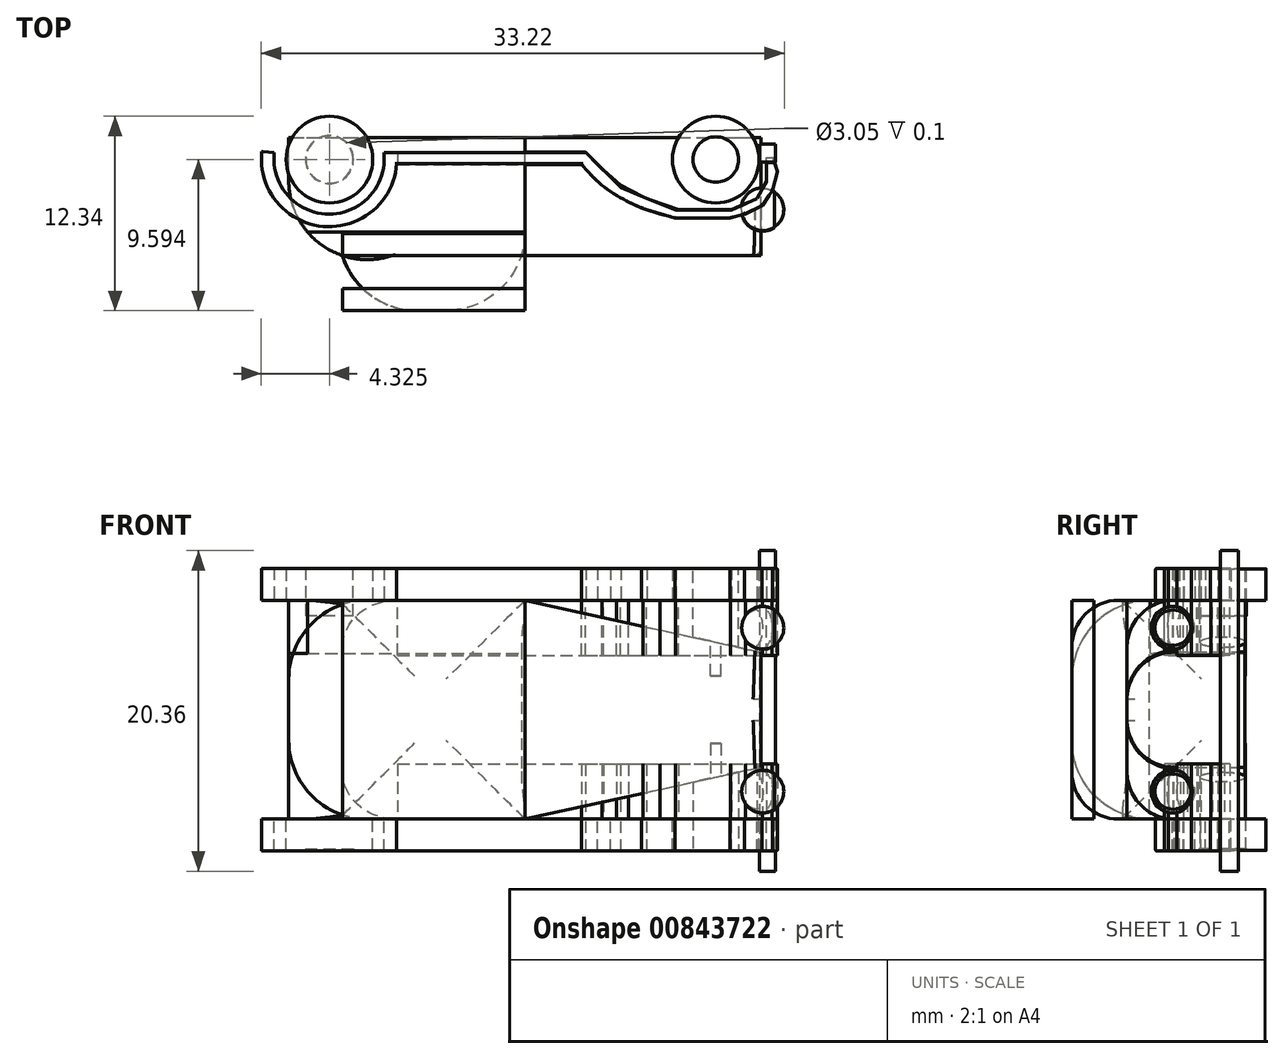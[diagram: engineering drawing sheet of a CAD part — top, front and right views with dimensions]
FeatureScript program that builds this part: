
annotation { "Feature Type Name" : "Feature", "Feature Type Description" : "" }
export const myFeature = defineFeature(function(context is Context, id is Id, definition is map)
    precondition{}
    {
        {
            var Q0;
            Q0=qCreatedBy(makeId("Front.planeOp"),FACE);
            var sketch = newSketch(context, id + "F0", { "sketchPlane" : qUnion([Q0])});
            skLineSegment(sketch, "E0", {"start": v(-15, 0) * mm, "end": v(-15, -6.95) * mm});
            skLineSegment(sketch, "E1", {"start": v(-15, -6.95) * mm, "end": v(0, -6.95) * mm});
            skLineSegment(sketch, "E2", {"start": v(0, -6.95) * mm, "end": v(15, -3.65) * mm});
            skPoint(sketch, "E3.end.orphan", {"position": v(14.2, 0) * mm});
            skLineSegment(sketch, "E4", {"start": v(15, -3.65) * mm, "end": v(15, 0) * mm});
            skLineSegment(sketch, "E5.MirrorCS", {"start": v(0, 6.95) * mm, "end": v(15, 3.65) * mm});
            skLineSegment(sketch, "E6.MirrorCS", {"start": v(-15, 6.95) * mm, "end": v(0, 6.95) * mm});
            skLineSegment(sketch, "E7.MirrorCS", {"start": v(-15, 0) * mm, "end": v(-15, 6.95) * mm});
            skLineSegment(sketch, "E8", {"start": v(15, 0) * mm, "end": v(15, 3.65) * mm});
            skSolve(sketch);
        }
        {
            var Q0;
            Q0=makeQuery(id+"F0.imprint","IMPRINT",FACE,{"disambiguationData":[TD([[makeQuery(id+"F0.imprint","IMPRINT",EDGE,{"derivedFrom":sQuery(id+"F0.wireOp",EDGE,"E0")}),1.0]])]});
            extrude(context, id + "F1", {"entities" : qUnion([Q0]), "depth" : 7.5 * mm, "offsetDistance" : 25 * mm});
        }
        {
            var Q0;
            Q0=makeQuery(id+"F1.opExtrude","CAP_FACE",FACE,{"disambiguationData":[OSD([sQuery(id+"F0.wireOp",EDGE,"E0"),sQuery(id+"F0.wireOp",EDGE,"E1"),sQuery(id+"F0.wireOp",EDGE,"E2"),sQuery(id+"F0.wireOp",EDGE,"E4"),sQuery(id+"F0.wireOp",EDGE,"E6.MirrorCS"),sQuery(id+"F0.wireOp",EDGE,"E7.MirrorCS"),sQuery(id+"F0.wireOp",EDGE,"E5.MirrorCS"),sQuery(id+"F0.wireOp",EDGE,"E8")])],"isStart":false});
            var sketch = newSketch(context, id + "F2", { "sketchPlane" : qUnion([Q0])});
            skLineSegment(sketch, "E9", {"start": v(-11.6, 6.95) * mm, "end": v(0, 6.95) * mm});
            skLineSegment(sketch, "E10", {"start": v(0, 6.95) * mm, "end": v(0, -6.95) * mm});
            skLineSegment(sketch, "E11", {"start": v(0, -6.95) * mm, "end": v(-11.6, -6.95) * mm});
            skLineSegment(sketch, "E12", {"start": v(-11.6, 6.95) * mm, "end": v(-11.6, -6.95) * mm});
            skLineSegment(sketch, "E13", {"start": v(-11.6, -6.95) * mm, "end": v(0, -6.95) * mm});
            skLineSegment(sketch, "E14", {"start": v(0, 6.95) * mm, "end": v(-11.6, 6.95) * mm});
            skSolve(sketch);
        }
        {
            var Q0;
            Q0 = qSketchRegion(id + "F2", true);
            extrude(context, id + "F3", {"entities" : qUnion([Q0]), "operationType" : NewBodyOperationType.ADD, "depth" : 3.5 * mm, "offsetDistance" : 25 * mm});
        }
        {
            var Q0;
            Q0=makeQuery(id+"F1.opExtrude","CAP_EDGE",EDGE,{"disambiguationData":[OSD([sQuery(id+"F0.wireOp",EDGE,"E2")])],"isStart":false});
            var Q1;
            Q1=makeQuery(id+"F1.opExtrude","CAP_EDGE",EDGE,{"disambiguationData":[OSD([sQuery(id+"F0.wireOp",EDGE,"E5.MirrorCS")])],"isStart":false});
            fillet(context, id + "F4", {"entities" : qUnion([Q0, Q1]), "radius" : 3 * mm, "tangentPropagation" : true, "allowEdgeOverflow" : false});
        }
        {
            var Q0;
            Q0=qCreatedBy(makeId("Top.planeOp"),FACE);
            cPlane(context, id + "F5", {"entities" : qUnion([Q0]), "cplaneType" : CPlaneType.OFFSET, "offset" : 6.95 * mm, "width" : 150 * mm, "height" : 150 * mm});
        }
        {
            var Q0;
            Q0=qCreatedBy(id+"F5.planeOp",FACE);
            var sketch = newSketch(context, id + "F6", { "sketchPlane" : qUnion([Q0])});
            skCircle(sketch, "E15", {"center": v(-12.41, -1.4) * mm, "radius": 2.75 * mm});
            skCircle(sketch, "E16", {"center": v(12.12, -1.4) * mm, "radius": 2.75 * mm});
            skSolve(sketch);
        }
        {
            var Q0;
            Q0=makeQuery(id+"F6.imprint","IMPRINT",FACE,{"disambiguationData":[TD([[makeQuery(id+"F6.imprint","IMPRINT",EDGE,{"derivedFrom":sQuery(id+"F6.wireOp",EDGE,"E15")}),1.0]])]});
            var Q1;
            Q1=makeQuery(id+"F6.imprint","IMPRINT",FACE,{"disambiguationData":[TD([[makeQuery(id+"F6.imprint","IMPRINT",EDGE,{"derivedFrom":sQuery(id+"F6.wireOp",EDGE,"E16")}),1.0]])]});
            extrude(context, id + "F7", {"entities" : qUnion([Q0, Q1]), "depth" : 2 * mm, "offsetDistance" : 25 * mm});
        }
        {
            var Q0;
            Q0=makeQuery(id+"F7.opExtrude","CAP_FACE",FACE,{"disambiguationData":[OSD([sQuery(id+"F6.wireOp",EDGE,"E16")])],"isStart":false});
            var sketch = newSketch(context, id + "F8", { "sketchPlane" : qUnion([Q0])});
            skCircle(sketch, "E17", {"center": v(12.12, -1.4) * mm, "radius": 1.45 * mm});
            skSolve(sketch);
        }
        {
            var Q0;
            Q0=makeQuery(id+"F8.imprint","IMPRINT",FACE,{"disambiguationData":[TD([[makeQuery(id+"F8.imprint","IMPRINT",EDGE,{"derivedFrom":sQuery(id+"F8.wireOp",EDGE,"E17")}),1.0]])]});
            extrude(context, id + "F9", {"entities" : qUnion([Q0]), "oppositeDirection" : true, "depth" : 6.8 * mm, "offsetDistance" : 25 * mm});
        }
        {
            var Q0;
            Q0=makeQuery(id+"F7.opExtrude","CAP_FACE",FACE,{"disambiguationData":[OSD([sQuery(id+"F6.wireOp",EDGE,"E15")])],"isStart":false});
            var sketch = newSketch(context, id + "F10", { "sketchPlane" : qUnion([Q0])});
            skCircle(sketch, "E18", {"center": v(-12.41, -1.4) * mm, "radius": 1.5 * mm});
            skSolve(sketch);
        }
        {
            var Q0;
            Q0 = qSketchRegion(id + "F10", true);
            extrude(context, id + "F11", {"entities" : qUnion([Q0]), "oppositeDirection" : true, "depth" : 3 * mm, "offsetDistance" : 25 * mm});
        }
        {
            var Q0;
            Q0=qCreatedBy(id+"F5.planeOp",FACE);
            var sketch = newSketch(context, id + "F12", { "sketchPlane" : qUnion([Q0])});
            skArc(sketch, "E19", {"start": v(4.42, -1.53) * mm, "mid": v(2.23, -1.15) * mm, "end": v(0, -1.17) * mm});
            skArc(sketch, "E20", {"start": v(4.35, -2.05) * mm, "mid": v(5.24, -2.97) * mm, "end": v(6.27, -3.75) * mm});
            skLineSegment(sketch, "E21", {"start": v(0, -1.17) * mm, "end": v(0, -1.5) * mm});
            skArc(sketch, "E22", {"start": v(6.27, -3.75) * mm, "mid": v(7.53, -4.53) * mm, "end": v(8.93, -5.03) * mm});
            skArc(sketch, "E23", {"start": v(4.42, -1.53) * mm, "mid": v(8.72, -4.22) * mm, "end": v(13.79, -4.37) * mm});
            skArc(sketch, "E24.trimOffspring", {"start": v(13.79, -4.37) * mm, "mid": v(13.95, -4.28) * mm, "end": v(14.12, -4.18) * mm});
            skArc(sketch, "E25", {"start": v(8.93, -5.03) * mm, "mid": v(11.37, -5.34) * mm, "end": v(13.79, -4.9) * mm});
            skPoint(sketch, "E26.orphan", {"position": v(12.08, -5.03) * mm});
            skPoint(sketch, "E27.end.orphan", {"position": v(15.48, -1.53) * mm});
            skArc(sketch, "E28", {"start": v(13.79, -4.37) * mm, "mid": v(15.05, -3.2) * mm, "end": v(15.48, -1.53) * mm});
            skPoint(sketch, "E29.orphan", {"position": v(16.59, -1.53) * mm});
            skPoint(sketch, "E30.end.orphan", {"position": v(14.68, -4.37) * mm});
            skArc(sketch, "E31", {"start": v(13.79, -4.9) * mm, "mid": v(15.31, -3.56) * mm, "end": v(15.48, -1.53) * mm});
            skArc(sketch, "E32", {"start": v(4.35, -2.05) * mm, "mid": v(2.2, -1.6) * mm, "end": v(0, -1.67) * mm});
            skSolve(sketch);
        }
        {
            var Q0;
            Q0=makeQuery(id+"F7.opExtrude","CAP_EDGE",EDGE,{"disambiguationData":[OSD([sQuery(id+"F6.wireOp",EDGE,"E15")])],"isStart":false});
            var Q1;
            Q1=makeQuery(id+"F7.opExtrude","CAP_EDGE",EDGE,{"disambiguationData":[OSD([sQuery(id+"F6.wireOp",EDGE,"E16")])],"isStart":false});
            var Q2;
            Q2=makeQuery(id+"F11.opExtrude","CAP_EDGE",EDGE,{"disambiguationData":[OSD([sQuery(id+"F10.wireOp",EDGE,"E18")])],"isStart":true});
            var Q3;
            Q3=makeQuery(id+"FjrpbqXbbdKvt6q_5.opExtrude","CAP_EDGE",EDGE,{"disambiguationData":[OSD([sQuery(id+"FPjQeDhQ1sIP3dD_5.wireOp",EDGE,"ihl9n7q3-jGDN-Yr5W-vJwh-xwX7iQdXkGvS")])],"isStart":false});
            var Q4;
            Q4=makeQuery(id+"FjrpbqXbbdKvt6q_5.opExtrude","CAP_EDGE",EDGE,{"disambiguationData":[OSD([sQuery(id+"FPjQeDhQ1sIP3dD_5.wireOp",EDGE,"kHjxuYsD-Xfu5-1Gbw-WZIV-gBsFbxcFxdOy")])],"isStart":false});
            fillet(context, id + "F13", {"entities" : qUnion([Q0, Q1, Q2, Q3, Q4]), "radius" : 0.02 * mm, "tangentPropagation" : true, "allowEdgeOverflow" : false});
        }
        {
            var Q0;
            Q0=makeQuery(id+"F12.imprint","IMPRINT",FACE,{"disambiguationData":[TD([[makeQuery(id+"F12.imprint","IMPRINT",EDGE,{"derivedFrom":sQuery(id+"F12.wireOp",EDGE,"E19")}),1.0]])]});
            var Q1;
            Q1=makeQuery(id+"F1.opExtrude","SWEPT_FACE",FACE,{"disambiguationData":[OSD([sQuery(id+"F0.wireOp",EDGE,"E5.MirrorCS")])]});
            extrude(context, id + "F14", {"entities" : qUnion([Q0, Q1]), "operationType" : NewBodyOperationType.ADD, "oppositeDirection" : true, "depth" : 5.5 * mm, "offsetDistance" : 25 * mm});
        }
        {
            var Q0;
            Q0=makeQuery(id+"F7.opExtrude","SWEPT_BODY",BODY,{"disambiguationData":[OSD([sQuery(id+"F6.wireOp",EDGE,"E16")])]});
            var Q1;
            Q1=makeQuery(id+"F1.opExtrude","SWEPT_BODY",BODY,{"disambiguationData":[OSD([sQuery(id+"F0.wireOp",EDGE,"E0"),sQuery(id+"F0.wireOp",EDGE,"E1"),sQuery(id+"F0.wireOp",EDGE,"E2"),sQuery(id+"F0.wireOp",EDGE,"E4"),sQuery(id+"F0.wireOp",EDGE,"E6.MirrorCS"),sQuery(id+"F0.wireOp",EDGE,"E7.MirrorCS"),sQuery(id+"F0.wireOp",EDGE,"E5.MirrorCS"),sQuery(id+"F0.wireOp",EDGE,"E8")])]});
            var Q2;
            Q2=makeQuery(id+"F7.opExtrude","SWEPT_BODY",BODY,{"disambiguationData":[OSD([sQuery(id+"F6.wireOp",EDGE,"E15")])]});
            var Q3;
            Q3=makeQuery(id+"F9.opExtrude","SWEPT_BODY",BODY,{"disambiguationData":[OSD([sQuery(id+"F8.wireOp",EDGE,"E17")])]});
            var Q4;
            Q4=qCreatedBy(makeId("Top.planeOp"),FACE);
            mirror(context, id + "F15", {"entities" : qUnion([Q0, Q1, Q2, Q3]), "mirrorPlane" : qUnion([Q4])});
        }
        {
            var Q0;
            Q0=qCreatedBy(makeId("Right.planeOp"),FACE);
            cPlane(context, id + "F16", {"entities" : qUnion([Q0]), "cplaneType" : CPlaneType.OFFSET, "offset" : 14.9 * mm, "width" : 150 * mm, "height" : 150 * mm});
        }
        {
            var Q0;
            Q0=qCreatedBy(id+"F16.planeOp",FACE);
            var sketch = newSketch(context, id + "F17", { "sketchPlane" : qUnion([Q0])});
            skLineSegment(sketch, "E33.bottom", {"start": v(-1.57, 10.1) * mm, "end": v(-0.42, 10.1) * mm});
            skLineSegment(sketch, "E33.top", {"start": v(-1.57, -10.26) * mm, "end": v(-0.42, -10.26) * mm});
            skLineSegment(sketch, "E33.left", {"start": v(-1.57, 10.1) * mm, "end": v(-1.57, -10.26) * mm});
            skLineSegment(sketch, "E33.right", {"start": v(-0.42, 10.1) * mm, "end": v(-0.42, -10.26) * mm});
            skSolve(sketch);
        }
        {
            var Q0;
            Q0=makeQuery(id+"F17.imprint","IMPRINT",FACE,{"disambiguationData":[TD([[makeQuery(id+"F17.imprint","IMPRINT",EDGE,{"derivedFrom":sQuery(id+"F17.wireOp",EDGE,"E33.bottom")}),-1.0]])]});
            extrude(context, id + "F18", {"entities" : qUnion([Q0]), "depth" : 1 * mm, "offsetDistance" : 25 * mm});
        }
        {
            var Q0;
            Q0=makeQuery(id+"F3.opExtrude","CAP_FACE",FACE,{"disambiguationData":[OSD([sQuery(id+"F2.wireOp",EDGE,"E9"),sQuery(id+"F2.wireOp",EDGE,"E10"),sQuery(id+"F2.wireOp",EDGE,"E11"),sQuery(id+"F2.wireOp",EDGE,"GGsqdMdr-Gb20-osrV-6Zm3-nt5zJUMAEgAM")])],"isStart":false});
            fillet(context, id + "F19", {"entities" : qUnion([Q0]), "radius" : 5 * mm, "tangentPropagation" : true, "allowEdgeOverflow" : false});
        }
        {
            var Q0;
            Q0 = qSketchRegion(id + "F2", true);
            var Q1;
            Q1=makeQuery(id+"F15.opPattern","COPY",FACE,{"derivedFrom":makeQuery(id+"F3.opExtrude","CAP_FACE",FACE,{"disambiguationData":[OSD([sQuery(id+"F2.wireOp",EDGE,"E10"),sQuery(id+"F2.wireOp",EDGE,"E12"),sQuery(id+"F2.wireOp",EDGE,"E13"),sQuery(id+"F2.wireOp",EDGE,"E14")])],"isStart":false}),"instanceName":"1"});
            extrude(context, id + "F20", {"entities" : qUnion([Q0, Q1]), "oppositeDirection" : true, "depth" : 1.4 * mm, "offsetDistance" : 25 * mm});
        }
        {
            var Q0;
            Q0=makeQuery(id+"F1.opExtrude","CAP_EDGE",EDGE,{"disambiguationData":[OSD([sQuery(id+"F0.wireOp",EDGE,"E0"),sQuery(id+"F0.wireOp",EDGE,"E7.MirrorCS")])],"isStart":false});
            fillet(context, id + "F21", {"entities" : qUnion([Q0]), "radius" : 5 * mm, "tangentPropagation" : true, "allowEdgeOverflow" : false});
        }
        {
            var Q0;
            Q0 = qSketchRegion(id + "F12", true);
            extrude(context, id + "F22", {"entities" : qUnion([Q0]), "oppositeDirection" : true, "depth" : 0.04 * mm, "offsetDistance" : 25 * mm});
        }
        {
            var Q0;
            Q0=qCreatedBy(id+"F5.planeOp",FACE);
            var sketch = newSketch(context, id + "F23", { "sketchPlane" : qUnion([Q0])});
            skLineSegment(sketch, "E34", {"start": v(-8.08, -0.95) * mm, "end": v(3.86, -0.95) * mm});
            skLineSegment(sketch, "E35", {"start": v(3.86, -0.95) * mm, "end": v(5, -2.08) * mm});
            skLineSegment(sketch, "E36", {"start": v(5, -2.08) * mm, "end": v(6.08, -3.03) * mm});
            skLineSegment(sketch, "E37", {"start": v(6.08, -3.03) * mm, "end": v(7.72, -3.9) * mm});
            skLineSegment(sketch, "E38", {"start": v(7.72, -3.9) * mm, "end": v(9.76, -4.58) * mm});
            skLineSegment(sketch, "E39", {"start": v(9.76, -4.58) * mm, "end": v(11.53, -4.58) * mm});
            skLineSegment(sketch, "E40", {"start": v(11.53, -4.58) * mm, "end": v(13.11, -4.58) * mm});
            skLineSegment(sketch, "E41", {"start": v(13.11, -4.58) * mm, "end": v(14.75, -3.9) * mm});
            skLineSegment(sketch, "E42", {"start": v(14.75, -3.9) * mm, "end": v(15.34, -2.8) * mm});
            skLineSegment(sketch, "E43", {"start": v(15.34, -2.8) * mm, "end": v(15.34, -1.3) * mm});
            skPoint(sketch, "E44.end.orphan", {"position": v(14.38, -4.58) * mm});
            skPoint(sketch, "E45.end.orphan", {"position": v(15.2, -3.9) * mm});
            skLineSegment(sketch, "E46", {"start": v(-8.1, -1.72) * mm, "end": v(3.59, -1.72) * mm});
            skLineSegment(sketch, "E47", {"start": v(15.34, -1.3) * mm, "end": v(15.74, -1.3) * mm});
            skArc(sketch, "E48.trimOffspring", {"start": v(-8.08, -0.95) * mm, "mid": v(-8.09, -0.9) * mm, "end": v(-8.1, -0.87) * mm});
            skPoint(sketch, "E49.start.orphan", {"position": v(15.74, -2.67) * mm});
            skLineSegment(sketch, "E50", {"start": v(3.59, -1.72) * mm, "end": v(4.91, -3) * mm});
            skLineSegment(sketch, "E51", {"start": v(4.91, -3) * mm, "end": v(5.8, -3.65) * mm});
            skLineSegment(sketch, "E52", {"start": v(5.8, -3.65) * mm, "end": v(6.59, -4.1) * mm});
            skLineSegment(sketch, "E53", {"start": v(6.59, -4.1) * mm, "end": v(7.5, -4.54) * mm});
            skLineSegment(sketch, "E54", {"start": v(7.5, -4.54) * mm, "end": v(8.58, -4.86) * mm});
            skLineSegment(sketch, "E55", {"start": v(8.58, -4.86) * mm, "end": v(9.58, -5.1) * mm});
            skLineSegment(sketch, "E56", {"start": v(9.58, -5.1) * mm, "end": v(10.66, -5.1) * mm});
            skLineSegment(sketch, "E57", {"start": v(10.66, -5.1) * mm, "end": v(11.98, -5.1) * mm});
            skLineSegment(sketch, "E58", {"start": v(11.98, -5.1) * mm, "end": v(13.06, -5.1) * mm});
            skLineSegment(sketch, "E59", {"start": v(13.06, -5.1) * mm, "end": v(14, -4.86) * mm});
            skLineSegment(sketch, "E60", {"start": v(14, -4.86) * mm, "end": v(15.08, -4.32) * mm});
            skLineSegment(sketch, "E61", {"start": v(15.08, -4.32) * mm, "end": v(15.7, -3.4) * mm});
            skLineSegment(sketch, "E62", {"start": v(15.7, -3.4) * mm, "end": v(16.05, -2.16) * mm});
            skLineSegment(sketch, "E63", {"start": v(16.05, -2.16) * mm, "end": v(15.74, -1.3) * mm});
            skLineSegment(sketch, "E64", {"start": v(-8.08, -0.95) * mm, "end": v(-8.1, -1.72) * mm});
            skSolve(sketch);
        }
        {
            var Q0;
            Q0=makeQuery(id+"F3.boolean.opBoolean","MERGE",FACE,{"derivedFrom":[makeQuery(id+"F1.opExtrude","SWEPT_FACE",FACE,{"disambiguationData":[OSD([sQuery(id+"F0.wireOp",EDGE,"E6.MirrorCS")])]}),makeQuery(id+"F3.opExtrude","SWEPT_FACE",FACE,{"disambiguationData":[OSD([sQuery(id+"F2.wireOp",EDGE,"E14")])]})]});
            extrude(context, id + "F24", {"entities" : qUnion([Q0]), "oppositeDirection" : true, "depth" : 3.4 * mm, "offsetDistance" : 25 * mm});
        }
        {
            var Q0;
            Q0=qCreatedBy(id+"F16.planeOp",FACE);
            cPlane(context, id + "F25", {"entities" : qUnion([Q0]), "cplaneType" : CPlaneType.OFFSET, "offset" : 2.7 * mm, "oppositeDirection" : true, "width" : 150 * mm, "height" : 150 * mm});
        }
        {
            var Q0;
            Q0=qCreatedBy(id+"F25.planeOp",FACE);
            var sketch = newSketch(context, id + "F26", { "sketchPlane" : qUnion([Q0])});
            skPoint(sketch, "E65.end.orphan", {"position": v(-3.96, 4.77) * mm});
            skPoint(sketch, "E65.start.orphan", {"position": v(-5.52, 4.77) * mm});
            skLineSegment(sketch, "E66", {"start": v(-5.83, 5.17) * mm, "end": v(-1.57, 5.17) * mm});
            skCircle(sketch, "E67", {"center": v(-3.96, 5.17) * mm, "radius": 0.9 * mm});
            skSolve(sketch);
        }
        {
            var Q0;
            Q0=makeQuery(id+"F23.imprint","IMPRINT",FACE,{"disambiguationData":[TD([[makeQuery(id+"F23.imprint","IMPRINT",EDGE,{"derivedFrom":sQuery(id+"F23.wireOp",EDGE,"E34")}),-1.0]])]});
            extrude(context, id + "F27", {"entities" : qUnion([Q0]), "oppositeDirection" : true, "depth" : 3.5 * mm, "offsetDistance" : 25 * mm});
        }
        {
            var Q0;
            Q0=qCreatedBy(id+"F5.planeOp",FACE);
            var sketch = newSketch(context, id + "F28", { "sketchPlane" : qUnion([Q0])});
            skLineSegment(sketch, "E68", {"start": v(0, -0.98) * mm, "end": v(-8.96, -0.98) * mm});
            skLineSegment(sketch, "E69", {"start": v(4.61, -1.71) * mm, "end": v(3.87, -0.98) * mm});
            skLineSegment(sketch, "E70", {"start": v(3.87, -0.98) * mm, "end": v(0, -0.98) * mm});
            skLineSegment(sketch, "E71", {"start": v(4.61, -1.71) * mm, "end": v(5.44, -2.52) * mm});
            skLineSegment(sketch, "E72", {"start": v(5.44, -2.52) * mm, "end": v(6.12, -3.19) * mm});
            skLineSegment(sketch, "E73", {"start": v(6.12, -3.19) * mm, "end": v(7.75, -3.9) * mm});
            skLineSegment(sketch, "E74", {"start": v(7.75, -3.9) * mm, "end": v(9.58, -4.6) * mm});
            skLineSegment(sketch, "E75", {"start": v(9.58, -4.6) * mm, "end": v(11.6, -4.6) * mm});
            skPoint(sketch, "E76.start.orphan", {"position": v(15.87, -1.71) * mm});
            skPoint(sketch, "E77.end.orphan", {"position": v(15.3, -1.71) * mm});
            skLineSegment(sketch, "E78", {"start": v(11.6, -4.6) * mm, "end": v(13.11, -4.6) * mm});
            skLineSegment(sketch, "E79", {"start": v(13.11, -4.6) * mm, "end": v(14.75, -3.88) * mm});
            skLineSegment(sketch, "E80", {"start": v(14.75, -3.88) * mm, "end": v(15.34, -2.8) * mm});
            skLineSegment(sketch, "E81", {"start": v(15.34, -2.8) * mm, "end": v(15.34, -1.6) * mm});
            skLineSegment(sketch, "E82", {"start": v(15.34, -1.6) * mm, "end": v(15.85, -1.6) * mm});
            skLineSegment(sketch, "E83", {"start": v(15.85, -1.6) * mm, "end": v(16.05, -2.18) * mm});
            skLineSegment(sketch, "E84", {"start": v(16.05, -2.18) * mm, "end": v(15.71, -3.4) * mm});
            skLineSegment(sketch, "E85", {"start": v(15.71, -3.4) * mm, "end": v(15.07, -4.33) * mm});
            skLineSegment(sketch, "E86", {"start": v(15.07, -4.33) * mm, "end": v(13.95, -4.87) * mm});
            skLineSegment(sketch, "E87", {"start": v(13.95, -4.87) * mm, "end": v(13.03, -5.1) * mm});
            skLineSegment(sketch, "E88", {"start": v(13.03, -5.1) * mm, "end": v(9.54, -5.1) * mm});
            skLineSegment(sketch, "E89", {"start": v(9.54, -5.1) * mm, "end": v(7.4, -4.48) * mm});
            skLineSegment(sketch, "E90", {"start": v(7.4, -4.48) * mm, "end": v(6.46, -4.03) * mm});
            skArc(sketch, "E91", {"start": v(3.59, -1.66) * mm, "mid": v(4.88, -3.02) * mm, "end": v(6.46, -4.03) * mm});
            skLineSegment(sketch, "E92", {"start": v(3.59, -1.66) * mm, "end": v(-8.14, -1.66) * mm});
            skArc(sketch, "E93", {"start": v(-15.91, -0.98) * mm, "mid": v(-12.44, -4.87) * mm, "end": v(-8.96, -0.98) * mm});
            skArc(sketch, "E94.0", {"start": v(-16.7, -0.89) * mm, "mid": v(-12.82, -5.65) * mm, "end": v(-8.14, -1.66) * mm});
            skLineSegment(sketch, "E95", {"start": v(-15.91, -0.98) * mm, "end": v(-16.7, -0.89) * mm});
            skArc(sketch, "E96.trimOffspring", {"start": v(-8.15, -0.98) * mm, "mid": v(-8.16, -0.93) * mm, "end": v(-8.16, -0.89) * mm});
            skLineSegment(sketch, "E97.trimOffspring", {"start": v(-8.95, -1.66) * mm, "end": v(-8.98, -1.66) * mm});
            skSolve(sketch);
        }
        {
            var Q0;
            Q0 = qSketchRegion(id + "F28", true);
            extrude(context, id + "F29", {"entities" : qUnion([Q0]), "depth" : 2.03 * mm, "offsetDistance" : 25 * mm});
        }
        {
            var Q0;
            Q0=makeQuery(id+"F29.opExtrude","SWEPT_BODY",BODY,{"disambiguationData":[OSD([sQuery(id+"F28.wireOp",EDGE,"E68"),sQuery(id+"F28.wireOp",EDGE,"E69"),sQuery(id+"F28.wireOp",EDGE,"E70"),sQuery(id+"F28.wireOp",EDGE,"E71"),sQuery(id+"F28.wireOp",EDGE,"E72"),sQuery(id+"F28.wireOp",EDGE,"E73"),sQuery(id+"F28.wireOp",EDGE,"E74"),sQuery(id+"F28.wireOp",EDGE,"E75"),sQuery(id+"F28.wireOp",EDGE,"E78"),sQuery(id+"F28.wireOp",EDGE,"E79"),sQuery(id+"F28.wireOp",EDGE,"E80"),sQuery(id+"F28.wireOp",EDGE,"E81"),sQuery(id+"F28.wireOp",EDGE,"E82"),sQuery(id+"F28.wireOp",EDGE,"E83"),sQuery(id+"F28.wireOp",EDGE,"E84"),sQuery(id+"F28.wireOp",EDGE,"E85"),sQuery(id+"F28.wireOp",EDGE,"E86"),sQuery(id+"F28.wireOp",EDGE,"E87"),sQuery(id+"F28.wireOp",EDGE,"E88"),sQuery(id+"F28.wireOp",EDGE,"E89"),sQuery(id+"F28.wireOp",EDGE,"E90"),sQuery(id+"F28.wireOp",EDGE,"E91"),sQuery(id+"F28.wireOp",EDGE,"E92"),sQuery(id+"F28.wireOp",EDGE,"E93"),sQuery(id+"F28.wireOp",EDGE,"E94.0"),sQuery(id+"F28.wireOp",EDGE,"E95")])]});
            var Q1;
            Q1=makeQuery(id+"F27.opExtrude","SWEPT_BODY",BODY,{"disambiguationData":[OSD([sQuery(id+"F23.wireOp",EDGE,"E34"),sQuery(id+"F23.wireOp",EDGE,"E35"),sQuery(id+"F23.wireOp",EDGE,"E36"),sQuery(id+"F23.wireOp",EDGE,"E37"),sQuery(id+"F23.wireOp",EDGE,"E38"),sQuery(id+"F23.wireOp",EDGE,"E39"),sQuery(id+"F23.wireOp",EDGE,"E40"),sQuery(id+"F23.wireOp",EDGE,"E41"),sQuery(id+"F23.wireOp",EDGE,"E42"),sQuery(id+"F23.wireOp",EDGE,"E43"),sQuery(id+"F23.wireOp",EDGE,"E46"),sQuery(id+"F23.wireOp",EDGE,"E47"),sQuery(id+"F23.wireOp",EDGE,"E50"),sQuery(id+"F23.wireOp",EDGE,"E51"),sQuery(id+"F23.wireOp",EDGE,"E52"),sQuery(id+"F23.wireOp",EDGE,"E53"),sQuery(id+"F23.wireOp",EDGE,"E54"),sQuery(id+"F23.wireOp",EDGE,"E55"),sQuery(id+"F23.wireOp",EDGE,"E56"),sQuery(id+"F23.wireOp",EDGE,"E57"),sQuery(id+"F23.wireOp",EDGE,"E58"),sQuery(id+"F23.wireOp",EDGE,"E59"),sQuery(id+"F23.wireOp",EDGE,"E60"),sQuery(id+"F23.wireOp",EDGE,"E61"),sQuery(id+"F23.wireOp",EDGE,"E62"),sQuery(id+"F23.wireOp",EDGE,"E63"),sQuery(id+"F23.wireOp",EDGE,"E64")])]});
            var Q2;
            Q2=qCreatedBy(makeId("Top.planeOp"),FACE);
            mirror(context, id + "F30", {"entities" : qUnion([Q0, Q1]), "mirrorPlane" : qUnion([Q2])});
        }
        {
            var Q0;
            Q0=makeQuery(id+"F27.opExtrude","SWEPT_FACE",FACE,{"disambiguationData":[OSD([sQuery(id+"F23.wireOp",EDGE,"E59")])]});
            var sketch = newSketch(context, id + "F31", { "sketchPlane" : qUnion([Q0])});
            skPoint(sketch, "E98.center.orphan", {"position": v(12.35, 5.2) * mm});
            skCircle(sketch, "E99", {"center": v(13.47, 5.2) * mm, "radius": 1.36 * mm});
            skLineSegment(sketch, "E100", {"start": v(13.52, 7.37) * mm, "end": v(13.47, 3.84) * mm});
            skSolve(sketch);
        }
        {
            var Q0;
            {var subQ0=sQuery(id+"F31.wireOp",EDGE,"E100");var subQ1=sQuery(id+"F31.wireOp",EDGE,"E99");var subQ6=makeQuery(id+"F31.imprint","INTERSECT",VERTEX,{"disambiguationData":[OD(0.0)],"derivedFrom":[subQ1,subQ0]});Q0=makeQuery(id+"F31.imprint","IMPRINT",FACE,{"disambiguationData":[TD([[makeQuery(id+"F31.imprint","IMPRINT",EDGE,{"disambiguationData":[TD([[subQ6,1.0]])],"derivedFrom":subQ0}),-1.0]])]});}
            var Q1;
            {var subQ0=sQuery(id+"F31.wireOp",EDGE,"E99");var subQ1=makeQuery(id+"F27.opExtrude","SWEPT_EDGE",EDGE,{"disambiguationData":[OSD([sQuery(id+"F23.wireOp",EDGE,"E59"),sQuery(id+"F23.wireOp",EDGE,"E60")])]});var subQ2=makeQuery(id+"F31.imprint","INTERSECT",VERTEX,{"disambiguationData":[OD(0.0)],"derivedFrom":[subQ1,subQ0]});Q1=makeQuery(id+"F31.imprint","IMPRINT",FACE,{"disambiguationData":[TD([[makeQuery(id+"F31.imprint","IMPRINT",EDGE,{"disambiguationData":[TD([[subQ2,-1.0]])],"derivedFrom":subQ0}),1.0]])]});}
            var Q2;
            Q2=sQuery(id+"F31.wireOp",EDGE,"E100");
            revolve(context, id + "F32", {"operationType" : NewBodyOperationType.ADD, "surfaceOperationType" : NewSurfaceOperationType.NEW, "entities" : qUnion([Q0, Q1]), "axis" : qUnion([Q2]), "revolveType" : RevolveType.FULL});
        }
        {
            var Q0;
            Q0=qCreatedBy(id+"F5.planeOp",FACE);
            var sketch = newSketch(context, id + "F33", { "sketchPlane" : qUnion([Q0])});
            skLineSegment(sketch, "E101", {"start": v(15.87, -3.4) * mm, "end": v(15.87, -5.83) * mm});
            skLineSegment(sketch, "E102", {"start": v(15.87, -5.83) * mm, "end": v(17.54, -5.83) * mm});
            skLineSegment(sketch, "E103", {"start": v(17.54, -5.83) * mm, "end": v(17.54, -3.13) * mm});
            skLineSegment(sketch, "E104", {"start": v(17.54, -3.13) * mm, "end": v(15.87, -3.4) * mm});
            skSolve(sketch);
        }
        {
            var Q0;
            Q0 = qSketchRegion(id + "F33", true);
            extrude(context, id + "F34", {"entities" : qUnion([Q0]), "operationType" : NewBodyOperationType.REMOVE, "oppositeDirection" : true, "depth" : 5.2 * mm, "offsetDistance" : 25 * mm});
        }
        {
            var Q0;
            Q0=makeQuery(id+"F27.opExtrude","SWEPT_BODY",BODY,{"disambiguationData":[OSD([sQuery(id+"F23.wireOp",EDGE,"E34"),sQuery(id+"F23.wireOp",EDGE,"E35"),sQuery(id+"F23.wireOp",EDGE,"E36"),sQuery(id+"F23.wireOp",EDGE,"E37"),sQuery(id+"F23.wireOp",EDGE,"E38"),sQuery(id+"F23.wireOp",EDGE,"E39"),sQuery(id+"F23.wireOp",EDGE,"E40"),sQuery(id+"F23.wireOp",EDGE,"E41"),sQuery(id+"F23.wireOp",EDGE,"E42"),sQuery(id+"F23.wireOp",EDGE,"E43"),sQuery(id+"F23.wireOp",EDGE,"E46"),sQuery(id+"F23.wireOp",EDGE,"E47"),sQuery(id+"F23.wireOp",EDGE,"E50"),sQuery(id+"F23.wireOp",EDGE,"E51"),sQuery(id+"F23.wireOp",EDGE,"E52"),sQuery(id+"F23.wireOp",EDGE,"E53"),sQuery(id+"F23.wireOp",EDGE,"E54"),sQuery(id+"F23.wireOp",EDGE,"E55"),sQuery(id+"F23.wireOp",EDGE,"E56"),sQuery(id+"F23.wireOp",EDGE,"E57"),sQuery(id+"F23.wireOp",EDGE,"E58"),sQuery(id+"F23.wireOp",EDGE,"E59"),sQuery(id+"F23.wireOp",EDGE,"E60"),sQuery(id+"F23.wireOp",EDGE,"E61"),sQuery(id+"F23.wireOp",EDGE,"E62"),sQuery(id+"F23.wireOp",EDGE,"E63"),sQuery(id+"F23.wireOp",EDGE,"E64")])]});
            var Q1;
            Q1=qCreatedBy(makeId("Top.planeOp"),FACE);
            mirror(context, id + "F35", {"entities" : qUnion([Q0]), "mirrorPlane" : qUnion([Q1])});
        }
        {
            var Q0;
            Q0=makeQuery(id+"F15.opPattern","COPY",FACE,{"derivedFrom":makeQuery(id+"F7.opExtrude","CAP_FACE",FACE,{"disambiguationData":[OSD([sQuery(id+"F6.wireOp",EDGE,"E15")])],"isStart":false}),"instanceName":"1"});
            var sketch = newSketch(context, id + "F36", { "sketchPlane" : qUnion([Q0])});
            skCircle(sketch, "E105", {"center": v(-12.41, 1.4) * mm, "radius": 1.52 * mm});
            skSolve(sketch);
        }
        {
            var Q0;
            Q0 = qSketchRegion(id + "F36", true);
            extrude(context, id + "F37", {"entities" : qUnion([Q0]), "operationType" : NewBodyOperationType.REMOVE, "oppositeDirection" : true, "depth" : 0.1 * mm, "offsetDistance" : 25 * mm});
        }
        {
            var Q0;
            Q0=makeQuery(id+"F15.opPattern","COPY",EDGE,{"derivedFrom":makeQuery(id+"F1.opExtrude","SWEPT_EDGE",EDGE,{"disambiguationData":[OSD([sQuery(id+"F0.wireOp",EDGE,"E0"),sQuery(id+"F0.wireOp",EDGE,"E1")])]}),"instanceName":"1"});
            var Q1;
            Q1=makeQuery(id+"F15.opPattern","COPY",EDGE,{"derivedFrom":makeQuery(id+"F1.opExtrude","SWEPT_EDGE",EDGE,{"disambiguationData":[OSD([sQuery(id+"F0.wireOp",EDGE,"E6.MirrorCS"),sQuery(id+"F0.wireOp",EDGE,"E7.MirrorCS")])]}),"instanceName":"1"});
            fillet(context, id + "F38", {"entities" : qUnion([Q0, Q1]), "radius" : 5 * mm, "tangentPropagation" : true, "allowEdgeOverflow" : false});
        }
        {
            var Q0;
            Q0=makeQuery(id+"F15.opPattern","COPY",EDGE,{"derivedFrom":makeQuery(id+"F3.opExtrude","CAP_EDGE",EDGE,{"disambiguationData":[OSD([sQuery(id+"F2.wireOp",EDGE,"E12")])],"isStart":false}),"instanceName":"1"});
            var Q1;
            Q1=makeQuery(id+"F15.opPattern","COPY",EDGE,{"derivedFrom":makeQuery(id+"F1.opExtrude","CAP_EDGE",EDGE,{"disambiguationData":[OSD([sQuery(id+"F0.wireOp",EDGE,"E0"),sQuery(id+"F0.wireOp",EDGE,"E7.MirrorCS")])],"isStart":false}),"instanceName":"1"});
            var Q2;
            {var subQ0=sQuery(id+"F0.wireOp",EDGE,"E6.MirrorCS");var subQ1=sQuery(id+"F0.wireOp",EDGE,"E1");var subQ2=sQuery(id+"F0.wireOp",EDGE,"E7.MirrorCS");var subQ3=sQuery(id+"F0.wireOp",EDGE,"E0");Q2=makeQuery(id+"F38.opFillet","BLEND_EDGE",EDGE,{"blendedFrom":[makeQuery(id+"F15.opPattern","COPY",EDGE,{"derivedFrom":makeQuery(id+"F1.opExtrude","SWEPT_EDGE",EDGE,{"disambiguationData":[OSD([subQ0,subQ2])]}),"instanceName":"1"}),makeQuery(id+"F15.opPattern","COPY",FACE,{"derivedFrom":makeQuery(id+"F3.boolean.opBoolean","SPLIT",FACE,{"disambiguationData":[TD([makeQuery(id+"F3.opExtrude","SWEPT_FACE",FACE,{"disambiguationData":[OSD([sQuery(id+"F2.wireOp",EDGE,"E12")])]})])],"derivedFrom":makeQuery(id+"F1.opExtrude","CAP_FACE",FACE,{"disambiguationData":[OSD([subQ3,subQ1,sQuery(id+"F0.wireOp",EDGE,"E2"),sQuery(id+"F0.wireOp",EDGE,"E4"),subQ0,subQ2,sQuery(id+"F0.wireOp",EDGE,"E5.MirrorCS"),sQuery(id+"F0.wireOp",EDGE,"E8")])],"isStart":false})}),"instanceName":"1"})],"blendedInto":[makeQuery(id+"F15.opPattern","COPY",FACE,{"derivedFrom":makeQuery(id+"F3.boolean.opBoolean","SPLIT",FACE,{"disambiguationData":[TD([makeQuery(id+"F3.opExtrude","SWEPT_FACE",FACE,{"disambiguationData":[OSD([sQuery(id+"F2.wireOp",EDGE,"E12")])]})])],"derivedFrom":makeQuery(id+"F1.opExtrude","CAP_FACE",FACE,{"disambiguationData":[OSD([subQ3,subQ1,sQuery(id+"F0.wireOp",EDGE,"E2"),sQuery(id+"F0.wireOp",EDGE,"E4"),subQ0,subQ2,sQuery(id+"F0.wireOp",EDGE,"E5.MirrorCS"),sQuery(id+"F0.wireOp",EDGE,"E8")])],"isStart":false})}),"instanceName":"1"})]});}
            var Q3;
            {var subQ0=sQuery(id+"F0.wireOp",EDGE,"E6.MirrorCS");var subQ1=sQuery(id+"F0.wireOp",EDGE,"E1");var subQ2=sQuery(id+"F0.wireOp",EDGE,"E7.MirrorCS");var subQ3=sQuery(id+"F0.wireOp",EDGE,"E0");Q3=makeQuery(id+"F38.opFillet","BLEND_EDGE",EDGE,{"blendedFrom":[makeQuery(id+"F15.opPattern","COPY",EDGE,{"derivedFrom":makeQuery(id+"F1.opExtrude","SWEPT_EDGE",EDGE,{"disambiguationData":[OSD([subQ3,subQ1])]}),"instanceName":"1"}),makeQuery(id+"F15.opPattern","COPY",FACE,{"derivedFrom":makeQuery(id+"F3.boolean.opBoolean","SPLIT",FACE,{"disambiguationData":[TD([makeQuery(id+"F3.opExtrude","SWEPT_FACE",FACE,{"disambiguationData":[OSD([sQuery(id+"F2.wireOp",EDGE,"E12")])]})])],"derivedFrom":makeQuery(id+"F1.opExtrude","CAP_FACE",FACE,{"disambiguationData":[OSD([subQ3,subQ1,sQuery(id+"F0.wireOp",EDGE,"E2"),sQuery(id+"F0.wireOp",EDGE,"E4"),subQ0,subQ2,sQuery(id+"F0.wireOp",EDGE,"E5.MirrorCS"),sQuery(id+"F0.wireOp",EDGE,"E8")])],"isStart":false})}),"instanceName":"1"})],"blendedInto":[makeQuery(id+"F15.opPattern","COPY",FACE,{"derivedFrom":makeQuery(id+"F3.boolean.opBoolean","SPLIT",FACE,{"disambiguationData":[TD([makeQuery(id+"F3.opExtrude","SWEPT_FACE",FACE,{"disambiguationData":[OSD([sQuery(id+"F2.wireOp",EDGE,"E12")])]})])],"derivedFrom":makeQuery(id+"F1.opExtrude","CAP_FACE",FACE,{"disambiguationData":[OSD([subQ3,subQ1,sQuery(id+"F0.wireOp",EDGE,"E2"),sQuery(id+"F0.wireOp",EDGE,"E4"),subQ0,subQ2,sQuery(id+"F0.wireOp",EDGE,"E5.MirrorCS"),sQuery(id+"F0.wireOp",EDGE,"E8")])],"isStart":false})}),"instanceName":"1"})]});}
            fillet(context, id + "F39", {"entities" : qUnion([Q0, Q1, Q2, Q3]), "radius" : 5 * mm, "tangentPropagation" : true, "allowEdgeOverflow" : false});
        }
        {
            var Q0;
            Q0=makeQuery(id+"F15.opPattern","COPY",EDGE,{"derivedFrom":makeQuery(id+"F3.opExtrude","CAP_EDGE",EDGE,{"disambiguationData":[OSD([sQuery(id+"F2.wireOp",EDGE,"E14")])],"isStart":false}),"instanceName":"1"});
            var Q1;
            Q1=makeQuery(id+"F15.opPattern","COPY",EDGE,{"derivedFrom":makeQuery(id+"F3.opExtrude","CAP_EDGE",EDGE,{"disambiguationData":[OSD([sQuery(id+"F2.wireOp",EDGE,"E13")])],"isStart":false}),"instanceName":"1"});
            var Q2;
            Q2=makeQuery(id+"F39.opFillet","BLEND_EDGE",EDGE,{"blendedFrom":[makeQuery(id+"F15.opPattern","COPY",EDGE,{"derivedFrom":makeQuery(id+"F3.opExtrude","CAP_EDGE",EDGE,{"disambiguationData":[OSD([sQuery(id+"F2.wireOp",EDGE,"E12")])],"isStart":false}),"instanceName":"1"}),makeQuery(id+"F15.opPattern","COPY",FACE,{"derivedFrom":makeQuery(id+"F3.boolean.opBoolean","MERGE",FACE,{"derivedFrom":[makeQuery(id+"F1.opExtrude","SWEPT_FACE",FACE,{"disambiguationData":[OSD([sQuery(id+"F0.wireOp",EDGE,"E6.MirrorCS")])]}),makeQuery(id+"F3.opExtrude","SWEPT_FACE",FACE,{"disambiguationData":[OSD([sQuery(id+"F2.wireOp",EDGE,"E14")])]})]}),"instanceName":"1"})],"blendedInto":[makeQuery(id+"F15.opPattern","COPY",FACE,{"derivedFrom":makeQuery(id+"F3.boolean.opBoolean","MERGE",FACE,{"derivedFrom":[makeQuery(id+"F1.opExtrude","SWEPT_FACE",FACE,{"disambiguationData":[OSD([sQuery(id+"F0.wireOp",EDGE,"E6.MirrorCS")])]}),makeQuery(id+"F3.opExtrude","SWEPT_FACE",FACE,{"disambiguationData":[OSD([sQuery(id+"F2.wireOp",EDGE,"E14")])]})]}),"instanceName":"1"})]});
            var Q3;
            Q3=makeQuery(id+"F39.opFillet","BLEND_EDGE",EDGE,{"blendedFrom":[makeQuery(id+"F15.opPattern","COPY",EDGE,{"derivedFrom":makeQuery(id+"F3.opExtrude","CAP_EDGE",EDGE,{"disambiguationData":[OSD([sQuery(id+"F2.wireOp",EDGE,"E12")])],"isStart":false}),"instanceName":"1"}),makeQuery(id+"F15.opPattern","COPY",FACE,{"derivedFrom":makeQuery(id+"F3.boolean.opBoolean","MERGE",FACE,{"derivedFrom":[makeQuery(id+"F1.opExtrude","SWEPT_FACE",FACE,{"disambiguationData":[OSD([sQuery(id+"F0.wireOp",EDGE,"E1")])]}),makeQuery(id+"F3.opExtrude","SWEPT_FACE",FACE,{"disambiguationData":[OSD([sQuery(id+"F2.wireOp",EDGE,"E13")])]})]}),"instanceName":"1"})],"blendedInto":[makeQuery(id+"F15.opPattern","COPY",FACE,{"derivedFrom":makeQuery(id+"F3.boolean.opBoolean","MERGE",FACE,{"derivedFrom":[makeQuery(id+"F1.opExtrude","SWEPT_FACE",FACE,{"disambiguationData":[OSD([sQuery(id+"F0.wireOp",EDGE,"E1")])]}),makeQuery(id+"F3.opExtrude","SWEPT_FACE",FACE,{"disambiguationData":[OSD([sQuery(id+"F2.wireOp",EDGE,"E13")])]})]}),"instanceName":"1"})]});
            fillet(context, id + "F40", {"entities" : qUnion([Q0, Q1, Q2, Q3]), "radius" : 3 * mm, "tangentPropagation" : true, "allowEdgeOverflow" : false});
        }
        {
            var Q0;
            Q0=makeQuery(id+"F40.opFillet","BLEND_EDGE",EDGE,{"blendedFrom":[makeQuery(id+"F15.opPattern","COPY",EDGE,{"derivedFrom":makeQuery(id+"F3.opExtrude","CAP_EDGE",EDGE,{"disambiguationData":[OSD([sQuery(id+"F2.wireOp",EDGE,"E14")])],"isStart":false}),"instanceName":"1"}),makeQuery(id+"F15.opPattern","COPY",FACE,{"derivedFrom":makeQuery(id+"F3.opExtrude","SWEPT_FACE",FACE,{"disambiguationData":[OSD([sQuery(id+"F2.wireOp",EDGE,"E10")])]}),"instanceName":"1"})],"blendedInto":[makeQuery(id+"F15.opPattern","COPY",FACE,{"derivedFrom":makeQuery(id+"F3.opExtrude","SWEPT_FACE",FACE,{"disambiguationData":[OSD([sQuery(id+"F2.wireOp",EDGE,"E10")])]}),"instanceName":"1"})]});
            var Q1;
            Q1=makeQuery(id+"F4.opFillet","BLEND_EDGE",EDGE,{"blendedFrom":[makeQuery(id+"F1.opExtrude","CAP_EDGE",EDGE,{"disambiguationData":[OSD([sQuery(id+"F0.wireOp",EDGE,"E5.MirrorCS")])],"isStart":false}),makeQuery(id+"F1.opExtrude","SWEPT_FACE",FACE,{"disambiguationData":[OSD([sQuery(id+"F0.wireOp",EDGE,"E4"),sQuery(id+"F0.wireOp",EDGE,"E8")])]})],"blendedInto":[makeQuery(id+"F1.opExtrude","SWEPT_FACE",FACE,{"disambiguationData":[OSD([sQuery(id+"F0.wireOp",EDGE,"E4"),sQuery(id+"F0.wireOp",EDGE,"E8")])]})]});
            var Q2;
            Q2=makeQuery(id+"F4.opFillet","BLEND_EDGE",EDGE,{"blendedFrom":[makeQuery(id+"F1.opExtrude","CAP_EDGE",EDGE,{"disambiguationData":[OSD([sQuery(id+"F0.wireOp",EDGE,"E2")])],"isStart":false}),makeQuery(id+"F1.opExtrude","SWEPT_FACE",FACE,{"disambiguationData":[OSD([sQuery(id+"F0.wireOp",EDGE,"E4"),sQuery(id+"F0.wireOp",EDGE,"E8")])]})],"blendedInto":[makeQuery(id+"F1.opExtrude","SWEPT_FACE",FACE,{"disambiguationData":[OSD([sQuery(id+"F0.wireOp",EDGE,"E4"),sQuery(id+"F0.wireOp",EDGE,"E8")])]})]});
            fillet(context, id + "F41", {"entities" : qUnion([Q0, Q1, Q2]), "radius" : 0.5 * mm, "tangentPropagation" : true, "allowEdgeOverflow" : false});
        }
        {
            var Q0;
            Q0=makeQuery(id+"F29.opExtrude","CAP_EDGE",EDGE,{"disambiguationData":[OSD([sQuery(id+"F28.wireOp",EDGE,"E91")])],"isStart":false});
            var Q1;
            Q1=makeQuery(id+"F29.opExtrude","CAP_EDGE",EDGE,{"disambiguationData":[OSD([sQuery(id+"F28.wireOp",EDGE,"E90")])],"isStart":false});
            var Q2;
            Q2=makeQuery(id+"F29.opExtrude","CAP_EDGE",EDGE,{"disambiguationData":[OSD([sQuery(id+"F28.wireOp",EDGE,"E89")])],"isStart":false});
            var Q3;
            Q3=makeQuery(id+"F29.opExtrude","CAP_EDGE",EDGE,{"disambiguationData":[OSD([sQuery(id+"F28.wireOp",EDGE,"E88")])],"isStart":false});
            var Q4;
            Q4=makeQuery(id+"F29.opExtrude","CAP_EDGE",EDGE,{"disambiguationData":[OSD([sQuery(id+"F28.wireOp",EDGE,"E86")])],"isStart":false});
            var Q5;
            Q5=makeQuery(id+"F29.opExtrude","CAP_EDGE",EDGE,{"disambiguationData":[OSD([sQuery(id+"F28.wireOp",EDGE,"E94.0")])],"isStart":false});
            var Q6;
            Q6=makeQuery(id+"F29.opExtrude","CAP_EDGE",EDGE,{"disambiguationData":[OSD([sQuery(id+"F28.wireOp",EDGE,"E87")])],"isStart":false});
            var Q7;
            Q7=makeQuery(id+"F29.opExtrude","CAP_EDGE",EDGE,{"disambiguationData":[OSD([sQuery(id+"F28.wireOp",EDGE,"E85")])],"isStart":false});
            var Q8;
            Q8=makeQuery(id+"F29.opExtrude","CAP_EDGE",EDGE,{"disambiguationData":[OSD([sQuery(id+"F28.wireOp",EDGE,"E84")])],"isStart":false});
            var Q9;
            Q9=makeQuery(id+"F29.opExtrude","CAP_EDGE",EDGE,{"disambiguationData":[OSD([sQuery(id+"F28.wireOp",EDGE,"E83")])],"isStart":false});
            var Q10;
            Q10=makeQuery(id+"F30.opPattern","COPY",EDGE,{"derivedFrom":makeQuery(id+"F29.opExtrude","CAP_EDGE",EDGE,{"disambiguationData":[OSD([sQuery(id+"F28.wireOp",EDGE,"E88")])],"isStart":false}),"instanceName":"1"});
            var Q11;
            Q11=makeQuery(id+"F30.opPattern","COPY",EDGE,{"derivedFrom":makeQuery(id+"F29.opExtrude","CAP_EDGE",EDGE,{"disambiguationData":[OSD([sQuery(id+"F28.wireOp",EDGE,"E94.0")])],"isStart":false}),"instanceName":"1"});
            var Q12;
            Q12=makeQuery(id+"F30.opPattern","COPY",EDGE,{"derivedFrom":makeQuery(id+"F29.opExtrude","CAP_EDGE",EDGE,{"disambiguationData":[OSD([sQuery(id+"F28.wireOp",EDGE,"E91")])],"isStart":false}),"instanceName":"1"});
            var Q13;
            Q13=makeQuery(id+"F30.opPattern","COPY",EDGE,{"derivedFrom":makeQuery(id+"F29.opExtrude","CAP_EDGE",EDGE,{"disambiguationData":[OSD([sQuery(id+"F28.wireOp",EDGE,"E90")])],"isStart":false}),"instanceName":"1"});
            var Q14;
            Q14=makeQuery(id+"F30.opPattern","COPY",EDGE,{"derivedFrom":makeQuery(id+"F29.opExtrude","CAP_EDGE",EDGE,{"disambiguationData":[OSD([sQuery(id+"F28.wireOp",EDGE,"E89")])],"isStart":false}),"instanceName":"1"});
            var Q15;
            Q15=makeQuery(id+"F30.opPattern","COPY",EDGE,{"derivedFrom":makeQuery(id+"F29.opExtrude","CAP_EDGE",EDGE,{"disambiguationData":[OSD([sQuery(id+"F28.wireOp",EDGE,"E87")])],"isStart":false}),"instanceName":"1"});
            var Q16;
            Q16=makeQuery(id+"F30.opPattern","COPY",EDGE,{"derivedFrom":makeQuery(id+"F29.opExtrude","CAP_EDGE",EDGE,{"disambiguationData":[OSD([sQuery(id+"F28.wireOp",EDGE,"E85")])],"isStart":false}),"instanceName":"1"});
            var Q17;
            Q17=makeQuery(id+"F30.opPattern","COPY",EDGE,{"derivedFrom":makeQuery(id+"F29.opExtrude","CAP_EDGE",EDGE,{"disambiguationData":[OSD([sQuery(id+"F28.wireOp",EDGE,"E84")])],"isStart":false}),"instanceName":"1"});
            var Q18;
            Q18=makeQuery(id+"F30.opPattern","COPY",EDGE,{"derivedFrom":makeQuery(id+"F29.opExtrude","CAP_EDGE",EDGE,{"disambiguationData":[OSD([sQuery(id+"F28.wireOp",EDGE,"E83")])],"isStart":false}),"instanceName":"1"});
            var Q19;
            Q19=makeQuery(id+"F30.opPattern","COPY",EDGE,{"derivedFrom":makeQuery(id+"F29.opExtrude","CAP_EDGE",EDGE,{"disambiguationData":[OSD([sQuery(id+"F28.wireOp",EDGE,"E86")])],"isStart":false}),"instanceName":"1"});
            var Q20;
            {var subQ0=sQuery(id+"F6.wireOp",EDGE,"E15");Q20=makeQuery(id+"F15.opPattern","COPY",EDGE,{"derivedFrom":makeQuery(id+"F13.opFillet","BLEND_EDGE",EDGE,{"blendedFrom":[makeQuery(id+"F7.opExtrude","CAP_EDGE",EDGE,{"disambiguationData":[OSD([subQ0])],"isStart":false}),makeQuery(id+"F7.opExtrude","SWEPT_FACE",FACE,{"disambiguationData":[OSD([subQ0])]})],"blendedInto":[makeQuery(id+"F7.opExtrude","SWEPT_FACE",FACE,{"disambiguationData":[OSD([subQ0])]})]}),"instanceName":"1"});}
            var Q21;
            {var subQ0=sQuery(id+"F6.wireOp",EDGE,"E16");Q21=makeQuery(id+"F15.opPattern","COPY",EDGE,{"derivedFrom":makeQuery(id+"F13.opFillet","BLEND_EDGE",EDGE,{"blendedFrom":[makeQuery(id+"F7.opExtrude","CAP_EDGE",EDGE,{"disambiguationData":[OSD([subQ0])],"isStart":false}),makeQuery(id+"F7.opExtrude","CAP_FACE",FACE,{"disambiguationData":[OSD([subQ0])],"isStart":false})],"blendedInto":[makeQuery(id+"F7.opExtrude","CAP_FACE",FACE,{"disambiguationData":[OSD([subQ0])],"isStart":false})]}),"instanceName":"1"});}
            var Q22;
            {var subQ0=sQuery(id+"F6.wireOp",EDGE,"E16");Q22=makeQuery(id+"F13.opFillet","BLEND_EDGE",EDGE,{"blendedFrom":[makeQuery(id+"F7.opExtrude","CAP_EDGE",EDGE,{"disambiguationData":[OSD([subQ0])],"isStart":false}),makeQuery(id+"F7.opExtrude","CAP_FACE",FACE,{"disambiguationData":[OSD([subQ0])],"isStart":false})],"blendedInto":[makeQuery(id+"F7.opExtrude","CAP_FACE",FACE,{"disambiguationData":[OSD([subQ0])],"isStart":false})]});}
            var Q23;
            {var subQ0=sQuery(id+"F6.wireOp",EDGE,"E15");Q23=makeQuery(id+"F13.opFillet","BLEND_EDGE",EDGE,{"blendedFrom":[makeQuery(id+"F7.opExtrude","CAP_EDGE",EDGE,{"disambiguationData":[OSD([subQ0])],"isStart":false}),makeQuery(id+"F7.opExtrude","CAP_FACE",FACE,{"disambiguationData":[OSD([subQ0])],"isStart":false})],"blendedInto":[makeQuery(id+"F7.opExtrude","CAP_FACE",FACE,{"disambiguationData":[OSD([subQ0])],"isStart":false})]});}
            fillet(context, id + "F42", {"entities" : qUnion([Q0, Q1, Q2, Q3, Q4, Q5, Q6, Q7, Q8, Q9, Q10, Q11, Q12, Q13, Q14, Q15, Q16, Q17, Q18, Q19, Q20, Q21, Q22, Q23]), "radius" : 0.09 * mm, "tangentPropagation" : true, "allowEdgeOverflow" : false});
        }
    });
